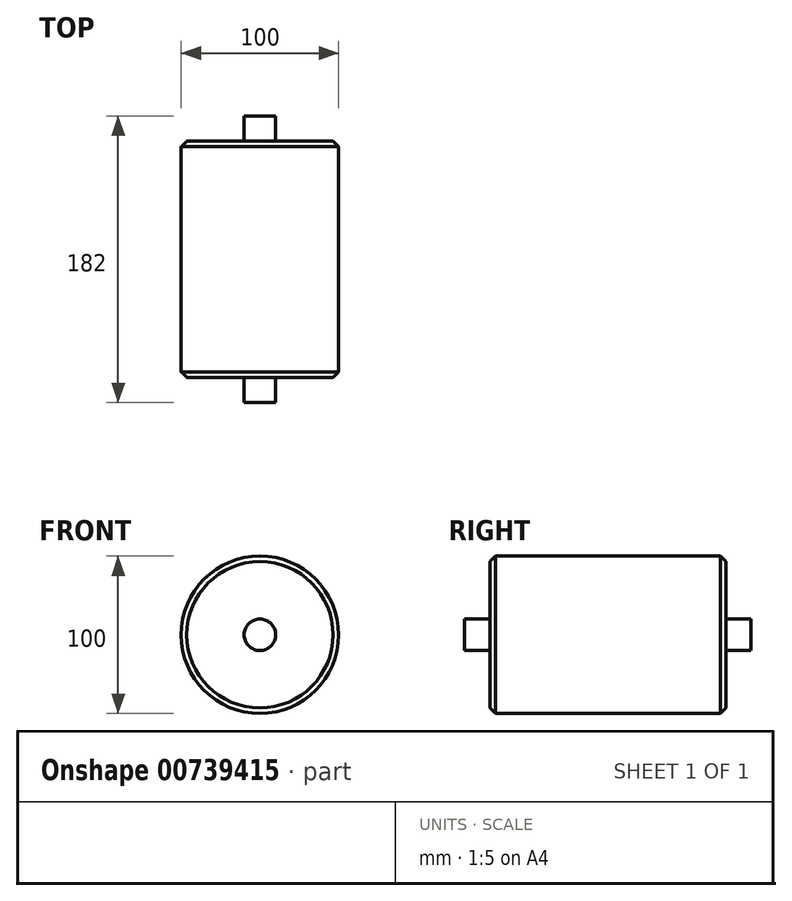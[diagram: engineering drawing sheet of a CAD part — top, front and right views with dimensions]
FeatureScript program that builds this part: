
annotation { "Feature Type Name" : "Feature", "Feature Type Description" : "" }
export const myFeature = defineFeature(function(context is Context, id is Id, definition is map)
    precondition{}
    {
        {
            var Q0;
            Q0=qCreatedBy(makeId("Top.planeOp"),FACE);
            var sketch = newSketch(context, id + "F0", { "sketchPlane" : qUnion([Q0])});
            skLineSegment(sketch, "E0.bottom", {"start": v(-101.47, 125.78) * mm, "end": v(-55, 125.78) * mm});
            skLineSegment(sketch, "E0.top", {"start": v(-101.47, -24.22) * mm, "end": v(-55, -24.22) * mm});
            skLineSegment(sketch, "E0.left", {"start": v(-105, 122.24) * mm, "end": v(-105, -20.69) * mm});
            skLineSegment(sketch, "E1", {"start": v(-55, 125.78) * mm, "end": v(-55, -173.95) * mm});
            skLineSegment(sketch, "E2.bottom", {"start": v(-55, -24.22) * mm, "end": v(-65, -24.22) * mm});
            skLineSegment(sketch, "E2.top", {"start": v(-55, -40.22) * mm, "end": v(-65, -40.22) * mm});
            skLineSegment(sketch, "E2.left", {"start": v(-55, -24.22) * mm, "end": v(-55, -40.22) * mm});
            skLineSegment(sketch, "E2.right", {"start": v(-65, -24.22) * mm, "end": v(-65, -40.22) * mm});
            skLineSegment(sketch, "E3.bottom", {"start": v(-55, 125.78) * mm, "end": v(-65, 125.78) * mm});
            skLineSegment(sketch, "E3.top", {"start": v(-55, 141.78) * mm, "end": v(-65, 141.78) * mm});
            skLineSegment(sketch, "E3.left", {"start": v(-55, 125.78) * mm, "end": v(-55, 141.78) * mm});
            skLineSegment(sketch, "E3.right", {"start": v(-65, 125.78) * mm, "end": v(-65, 141.78) * mm});
            skLineSegment(sketch, "E4", {"start": v(-105, 122.24) * mm, "end": v(-101.47, 125.78) * mm});
            skPoint(sketch, "E5.orphan", {"position": v(-105, 125.78) * mm});
            skLineSegment(sketch, "E6", {"start": v(-105, -20.69) * mm, "end": v(-101.47, -24.22) * mm});
            skPoint(sketch, "E7.orphan", {"position": v(-105, -24.22) * mm});
            skPoint(sketch, "E0.right.end.orphan", {"position": v(-5, -24.22) * mm});
            skPoint(sketch, "E8.orphan", {"position": v(-5, 125.78) * mm});
            skSolve(sketch);
        }
        {
            var Q0;
            Q0=makeQuery(id+"F0.imprint","IMPRINT",FACE,{"disambiguationData":[TD([[makeQuery(id+"F0.imprint","IMPRINT",EDGE,{"derivedFrom":sQuery(id+"F0.wireOp",EDGE,"E3.top")}),1.0]])]});
            var Q1;
            Q1=makeQuery(id+"F0.imprint","IMPRINT",FACE,{"disambiguationData":[TD([[makeQuery(id+"F0.imprint","IMPRINT",EDGE,{"derivedFrom":sQuery(id+"F0.wireOp",EDGE,"E0.left")}),1.0]])]});
            var Q2;
            {var subQ4=sQuery(id+"F0.wireOp",EDGE,"E2.top");Q2=makeQuery(id+"F0.imprint","IMPRINT",FACE,{"disambiguationData":[TD([[makeQuery(id+"F0.imprint","IMPRINT",EDGE,{"derivedFrom":subQ4}),-1.0]])]});}
            var Q3;
            Q3=sQuery(id+"F0.wireOp",EDGE,"E1");
            revolve(context, id + "F1", {"surfaceOperationType" : NewSurfaceOperationType.NEW, "entities" : qUnion([Q0, Q1, Q2]), "axis" : qUnion([Q3]), "revolveType" : RevolveType.FULL});
        }
    });
